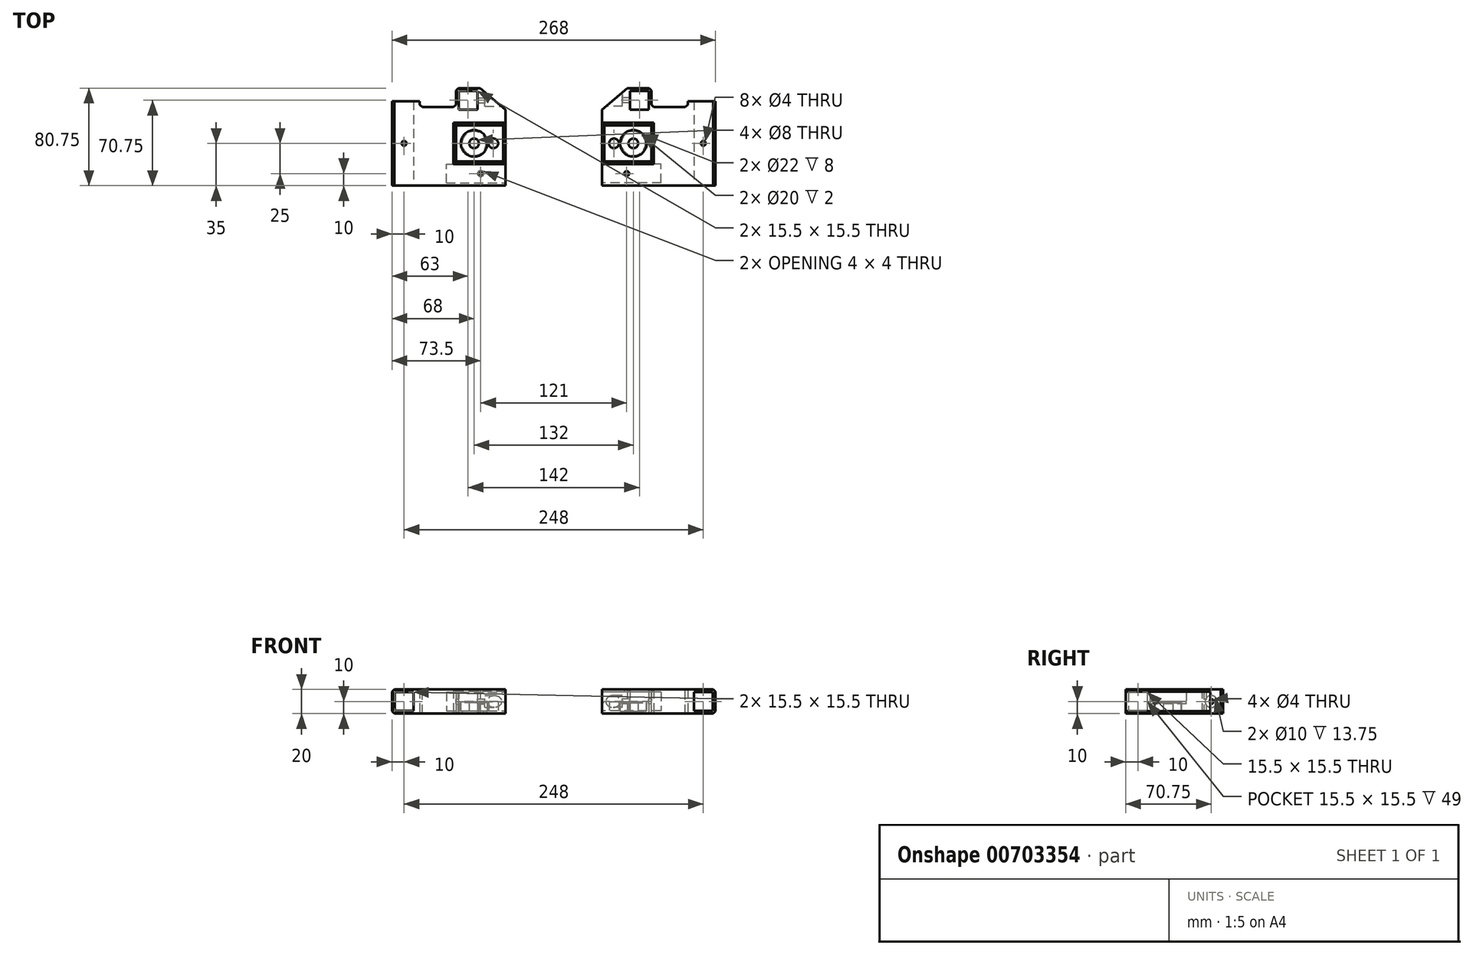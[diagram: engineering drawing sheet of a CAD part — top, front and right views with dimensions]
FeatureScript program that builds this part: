
annotation { "Feature Type Name" : "Feature", "Feature Type Description" : "" }
export const myFeature = defineFeature(function(context is Context, id is Id, definition is map)
    precondition{}
    {
        {
            var Q0;
            Q0=qCreatedBy(makeId("Top.planeOp"),FACE);
            var sketch = newSketch(context, id + "F0", { "sketchPlane" : qUnion([Q0])});
            skCircle(sketch, "E0", {"center": v(-50, 0) * mm, "radius": 4 * mm});
            skCircle(sketch, "E1", {"center": v(-66, 0) * mm, "radius": 4 * mm});
            skLineSegment(sketch, "E2.bottom", {"start": v(-81, 15) * mm, "end": v(-40, 15) * mm});
            skLineSegment(sketch, "E2.top", {"start": v(-81, -15) * mm, "end": v(-40, -15) * mm});
            skLineSegment(sketch, "E2.left", {"start": v(-81, 15) * mm, "end": v(-81, -15) * mm});
            skLineSegment(sketch, "E2.right", {"start": v(-40, 15) * mm, "end": v(-40, -15) * mm});
            skCircle(sketch, "E3", {"center": v(-66, 0) * mm, "radius": 11 * mm});
            skCircle(sketch, "E4", {"center": v(-66, 0) * mm, "radius": 10 * mm});
            skLineSegment(sketch, "E5", {"start": v(-81, 15) * mm, "end": v(-81, 35) * mm});
            skLineSegment(sketch, "E6", {"start": v(-81, -15) * mm, "end": v(-81, -35) * mm});
            skLineSegment(sketch, "E7", {"start": v(-81, -35) * mm, "end": v(-40, -35) * mm});
            skLineSegment(sketch, "E8", {"start": v(-40, -35) * mm, "end": v(-40, -15) * mm});
            skLineSegment(sketch, "E9.MirrorCS", {"start": v(-81, -35) * mm, "end": v(-40, -15) * mm, "construction": true});
            skCircle(sketch, "E10.MirrorC", {"center": v(-60.5, -25) * mm, "radius": 2 * mm});
            skLineSegment(sketch, "E11", {"start": v(-81, 35) * mm, "end": v(-134, 35) * mm});
            skLineSegment(sketch, "E12", {"start": v(-134, 35) * mm, "end": v(-134, -35) * mm});
            skLineSegment(sketch, "E13", {"start": v(-134, -35) * mm, "end": v(-81, -35) * mm});
            skLineSegment(sketch, "E14.bottom", {"start": v(-131.75, 7.75) * mm, "end": v(-116.25, 7.75) * mm});
            skLineSegment(sketch, "E14.top", {"start": v(-131.75, -7.75) * mm, "end": v(-116.25, -7.75) * mm});
            skLineSegment(sketch, "E14.left", {"start": v(-131.75, 7.75) * mm, "end": v(-131.75, -7.75) * mm});
            skLineSegment(sketch, "E14.right", {"start": v(-116.25, 7.75) * mm, "end": v(-116.25, -7.75) * mm});
            skPoint(sketch, "E14.middle", {"position": v(-124, 0) * mm});
            skCircle(sketch, "E15", {"center": v(-124, 0) * mm, "radius": 2 * mm});
            skLineSegment(sketch, "E16", {"start": v(-81, -15) * mm, "end": v(-40, -35) * mm, "construction": true});
            skLineSegment(sketch, "E17", {"start": v(-40, 15) * mm, "end": v(-40, 28) * mm});
            skLineSegment(sketch, "E18.top", {"start": v(-81, 45.75) * mm, "end": v(-61, 45.75) * mm});
            skLineSegment(sketch, "E18.left", {"start": v(-81, 35) * mm, "end": v(-81, 45.75) * mm});
            skLineSegment(sketch, "E18.right", {"start": v(-61, 28) * mm, "end": v(-61, 45.75) * mm});
            skLineSegment(sketch, "E19", {"start": v(-61, 28) * mm, "end": v(-40, 28) * mm});
            skLineSegment(sketch, "E20", {"start": v(-71, 45.75) * mm, "end": v(-71, 15) * mm, "construction": true});
            skLineSegment(sketch, "E21.bottom", {"start": v(-78.75, 43.5) * mm, "end": v(-63.25, 43.5) * mm});
            skLineSegment(sketch, "E21.top", {"start": v(-78.75, 28) * mm, "end": v(-63.25, 28) * mm});
            skLineSegment(sketch, "E21.left", {"start": v(-78.75, 43.5) * mm, "end": v(-78.75, 28) * mm});
            skLineSegment(sketch, "E21.right", {"start": v(-63.25, 43.5) * mm, "end": v(-63.25, 28) * mm});
            skPoint(sketch, "E21.middle", {"position": v(-71, 35.75) * mm});
            skLineSegment(sketch, "E22", {"start": v(-61, 45.75) * mm, "end": v(-40, 28) * mm});
            skLineSegment(sketch, "E23", {"start": v(-111, 35) * mm, "end": v(-111, 30) * mm});
            skLineSegment(sketch, "E24", {"start": v(-111, 30) * mm, "end": v(-81, 30) * mm});
            skSolve(sketch);
        }
        {
            var Q0;
            Q0=makeQuery(id+"F0.imprint","IMPRINT",FACE,{"disambiguationData":[TD([[makeQuery(id+"F0.imprint","IMPRINT",EDGE,{"derivedFrom":sQuery(id+"F0.wireOp",EDGE,"E0")}),-1.0]])]});
            extrude(context, id + "F1", {"entities" : qUnion([Q0]), "depth" : 10 * mm, "offsetDistance" : 25 * mm});
        }
        {
            var Q0;
            Q0=makeQuery(id+"F0.imprint","IMPRINT",FACE,{"disambiguationData":[TD([[makeQuery(id+"F0.imprint","IMPRINT",EDGE,{"derivedFrom":sQuery(id+"F0.wireOp",EDGE,"E2.bottom")}),1.0]])]});
            var Q1;
            Q1=makeQuery(id+"F0.imprint","IMPRINT",FACE,{"disambiguationData":[TD([[makeQuery(id+"F0.imprint","IMPRINT",EDGE,{"derivedFrom":sQuery(id+"F0.wireOp",EDGE,"E2.top")}),-1.0]])]});
            var Q2;
            Q2=makeQuery(id+"F0.imprint","IMPRINT",FACE,{"disambiguationData":[TD([[makeQuery(id+"F0.imprint","IMPRINT",EDGE,{"derivedFrom":sQuery(id+"F0.wireOp",EDGE,"E2.left")}),-1.0]])]});
            var Q3;
            Q3=makeQuery(id+"F0.imprint","IMPRINT",FACE,{"disambiguationData":[TD([[makeQuery(id+"F0.imprint","IMPRINT",EDGE,{"derivedFrom":sQuery(id+"F0.wireOp",EDGE,"E14.bottom")}),-1.0]])]});
            var Q4;
            {var subQ3=sQuery(id+"F0.wireOp",EDGE,"E18.bottom");Q4=makeQuery(id+"F0.imprint","IMPRINT",FACE,{"disambiguationData":[TD([[makeQuery(id+"F0.imprint","IMPRINT",EDGE,{"derivedFrom":subQ3}),1.0]])]});}
            var Q5;
            Q5=makeQuery(id+"F0.imprint","IMPRINT",FACE,{"disambiguationData":[TD([[makeQuery(id+"F0.imprint","IMPRINT",EDGE,{"derivedFrom":sQuery(id+"F0.wireOp",EDGE,"E18.right")}),-1.0]])]});
            extrude(context, id + "F2", {"entities" : qUnion([Q0, Q1, Q2, Q3, Q4, Q5]), "operationType" : NewBodyOperationType.ADD, "depth" : 20 * mm, "offsetDistance" : 25 * mm});
        }
        {
            var Q0;
            Q0=makeQuery(id+"F0.imprint","IMPRINT",FACE,{"disambiguationData":[TD([[makeQuery(id+"F0.imprint","IMPRINT",EDGE,{"derivedFrom":sQuery(id+"F0.wireOp",EDGE,"E3")}),1.0]])]});
            extrude(context, id + "F3", {"entities" : qUnion([Q0]), "operationType" : NewBodyOperationType.ADD, "depth" : 2 * mm, "offsetDistance" : 25 * mm});
        }
        {
            var Q0;
            Q0=makeQuery(id+"F1.opExtrude","SWEPT_FACE",FACE,{"disambiguationData":[OSD([sQuery(id+"F0.wireOp",EDGE,"E2.right"),sQuery(id+"F0.wireOp",EDGE,"lnFxAALh-jdBc-A6U8-vroT-Qa4E6eDd7EjD")])]});
            var sketch = newSketch(context, id + "F4", { "sketchPlane" : qUnion([Q0])});
            skPoint(sketch, "E25.MirrorP", {"position": v(-25, 10) * mm});
            skLineSegment(sketch, "E26.bottom", {"start": v(-32.75, 17.75) * mm, "end": v(-17.25, 17.75) * mm});
            skLineSegment(sketch, "E26.top", {"start": v(-32.75, 2.25) * mm, "end": v(-17.25, 2.25) * mm});
            skLineSegment(sketch, "E26.left", {"start": v(-32.75, 17.75) * mm, "end": v(-32.75, 2.25) * mm});
            skLineSegment(sketch, "E26.right", {"start": v(-17.25, 17.75) * mm, "end": v(-17.25, 2.25) * mm});
            skSolve(sketch);
        }
        {
            var Q0;
            Q0=makeQuery(id+"F4.imprint","IMPRINT",FACE,{"disambiguationData":[TD([[makeQuery(id+"F4.imprint","IMPRINT",EDGE,{"derivedFrom":sQuery(id+"F4.wireOp",EDGE,"jqq9uEYE-Uu8Z-dqdK-GRFn-HQd5PF9UBxML.bottom")}),-1.0]])]});
            var Q1;
            Q1=makeQuery(id+"F4.imprint","IMPRINT",FACE,{"disambiguationData":[TD([[makeQuery(id+"F4.imprint","IMPRINT",EDGE,{"derivedFrom":sQuery(id+"F4.wireOp",EDGE,"87533c7f-0075-4deb-97ef-fb3679262ebe1.MirrorCS")}),1.0]])]});
            var Q2;
            Q2=makeQuery(id+"F4.imprint","IMPRINT",FACE,{"disambiguationData":[TD([[makeQuery(id+"F4.imprint","IMPRINT",EDGE,{"derivedFrom":sQuery(id+"F4.wireOp",EDGE,"E26.bottom")}),-1.0]])]});
            extrude(context, id + "F5", {"entities" : qUnion([Q0, Q1, Q2]), "operationType" : NewBodyOperationType.REMOVE, "oppositeDirection" : true, "depth" : 49 * mm, "offsetDistance" : 25 * mm});
        }
        {
            var Q0;
            Q0=makeQuery(id+"F1.opExtrude","CAP_FACE",FACE,{"disambiguationData":[OSD([sQuery(id+"F0.wireOp",EDGE,"E0"),sQuery(id+"F0.wireOp",EDGE,"E2.top"),sQuery(id+"F0.wireOp",EDGE,"E2.left"),sQuery(id+"F0.wireOp",EDGE,"E2.right"),sQuery(id+"F0.wireOp",EDGE,"E3"),sQuery(id+"F0.wireOp",EDGE,"E5"),sQuery(id+"F0.wireOp",EDGE,"MvoQS5Ci-Blhk-AmRJ-KyyR-INJTXiuXo2vU"),sQuery(id+"F0.wireOp",EDGE,"lnFxAALh-jdBc-A6U8-vroT-Qa4E6eDd7EjD")])],"isStart":false});
            var sketch = newSketch(context, id + "F6", { "sketchPlane" : qUnion([Q0])});
            skCircle(sketch, "E27", {"center": v(-66, 0) * mm, "radius": 12.5 * mm});
            skSolve(sketch);
        }
        {
            var Q0;
            Q0=makeQuery(id+"F6.imprint","IMPRINT",FACE,{"disambiguationData":[TD([[makeQuery(id+"F6.imprint","IMPRINT",EDGE,{"derivedFrom":makeQuery(id+"F1.opExtrude","CAP_EDGE",EDGE,{"disambiguationData":[OSD([sQuery(id+"F0.wireOp",EDGE,"E3")])],"isStart":false})}),1.0]])]});
            extrude(context, id + "F7", {"entities" : qUnion([Q0]), "oppositeDirection" : true, "depth" : 8 * mm, "offsetDistance" : 25 * mm, "hasSecondDirection" : true, "secondDirectionOppositeDirection" : true, "secondDirectionDepth" : 1 * mm});
        }
        {
            var Q0;
            Q0=makeQuery(id+"F0.imprint","IMPRINT",FACE,{"disambiguationData":[TD([[makeQuery(id+"F0.imprint","IMPRINT",EDGE,{"derivedFrom":sQuery(id+"F0.wireOp",EDGE,"E1")}),1.0]])]});
            extrude(context, id + "F8", {"entities" : qUnion([Q0]), "operationType" : NewBodyOperationType.REMOVE, "depth" : 25 * mm, "offsetDistance" : 25 * mm});
        }
        {
            var Q0;
            Q0=makeQuery(id+"F2.opExtrude","SWEPT_FACE",FACE,{"disambiguationData":[OSD([sQuery(id+"F0.wireOp",EDGE,"E7"),sQuery(id+"F0.wireOp",EDGE,"E13")])]});
            var sketch = newSketch(context, id + "F9", { "sketchPlane" : qUnion([Q0])});
            skLineSegment(sketch, "E28.bottom", {"start": v(-116.25, 2.25) * mm, "end": v(-131.75, 2.25) * mm});
            skLineSegment(sketch, "E28.top", {"start": v(-116.25, 17.75) * mm, "end": v(-131.75, 17.75) * mm});
            skLineSegment(sketch, "E28.left", {"start": v(-116.25, 2.25) * mm, "end": v(-116.25, 17.75) * mm});
            skLineSegment(sketch, "E28.right", {"start": v(-131.75, 2.25) * mm, "end": v(-131.75, 17.75) * mm});
            skPoint(sketch, "E28.middle", {"position": v(-124, 10) * mm});
            skSolve(sketch);
        }
        {
            var Q0;
            Q0=makeQuery(id+"F9.imprint","IMPRINT",FACE,{"disambiguationData":[TD([[makeQuery(id+"F9.imprint","IMPRINT",EDGE,{"derivedFrom":sQuery(id+"F9.wireOp",EDGE,"E28.bottom")}),-1.0]])]});
            extrude(context, id + "F10", {"entities" : qUnion([Q0]), "operationType" : NewBodyOperationType.REMOVE, "endBound" : BoundingType.THROUGH_ALL, "oppositeDirection" : true, "depth" : 25 * mm, "offsetDistance" : 25 * mm});
        }
        {
            var Q0;
            Q0=makeQuery(id+"F2.opExtrude","CAP_EDGE",EDGE,{"disambiguationData":[OSD([sQuery(id+"F0.wireOp",EDGE,"E2.left")])],"isStart":false});
            var Q1;
            Q1=makeQuery(id+"F2.opExtrude","CAP_EDGE",EDGE,{"disambiguationData":[OSD([sQuery(id+"F0.wireOp",EDGE,"E2.bottom")])],"isStart":false});
            var Q2;
            Q2=makeQuery(id+"F2.opExtrude","CAP_EDGE",EDGE,{"disambiguationData":[OSD([sQuery(id+"F0.wireOp",EDGE,"E2.top")])],"isStart":false});
            var Q3;
            Q3=makeQuery(id+"F2.opExtrude","CAP_EDGE",EDGE,{"disambiguationData":[OSD([sQuery(id+"F0.wireOp",EDGE,"E12")])],"isStart":false});
            var Q4;
            Q4=makeQuery(id+"F2.opExtrude","CAP_EDGE",EDGE,{"disambiguationData":[OSD([sQuery(id+"F0.wireOp",EDGE,"E12")])],"isStart":true});
            var Q5;
            Q5=makeQuery(id+"F1.opExtrude","CAP_EDGE",EDGE,{"disambiguationData":[OSD([sQuery(id+"F0.wireOp",EDGE,"E2.right")])],"isStart":false});
            var Q6;
            Q6=makeQuery(id+"F2.opExtrude","SWEPT_EDGE",EDGE,{"disambiguationData":[OSD([sQuery(id+"F0.wireOp",EDGE,"E23"),sQuery(id+"F0.wireOp",EDGE,"E24")])]});
            var Q7;
            Q7=makeQuery(id+"F2.opExtrude","SWEPT_EDGE",EDGE,{"disambiguationData":[OSD([sQuery(id+"F0.wireOp",EDGE,"E5"),sQuery(id+"F0.wireOp",EDGE,"E24")])]});
            var Q8;
            Q8=makeQuery(id+"F2.opExtrude","SWEPT_EDGE",EDGE,{"disambiguationData":[OSD([sQuery(id+"F0.wireOp",EDGE,"E18.top"),sQuery(id+"F0.wireOp",EDGE,"E18.left")])]});
            chamfer(context, id + "F11", {"entities" : qUnion([Q0, Q1, Q2, Q3, Q4, Q5, Q6, Q7, Q8]), "width" : 2 * mm, "tangentPropagation" : true});
        }
        {
            var Q0;
            Q0=makeQuery(id+"F2.boolean.opBoolean","MERGE",FACE,{"derivedFrom":[makeQuery(id+"F1.opExtrude","SWEPT_FACE",FACE,{"disambiguationData":[OSD([sQuery(id+"F0.wireOp",EDGE,"E2.right")])]}),makeQuery(id+"F2.opExtrude","SWEPT_FACE",FACE,{"disambiguationData":[OSD([sQuery(id+"F0.wireOp",EDGE,"E8")])]}),makeQuery(id+"F2.opExtrude","SWEPT_FACE",FACE,{"disambiguationData":[OSD([sQuery(id+"F0.wireOp",EDGE,"E17")])]})]});
            var sketch = newSketch(context, id + "F12", { "sketchPlane" : qUnion([Q0])});
            skCircle(sketch, "E29", {"center": v(35.75, 10) * mm, "radius": 5 * mm});
            skCircle(sketch, "E30", {"center": v(35.75, 10) * mm, "radius": 2 * mm});
            skSolve(sketch);
        }
        {
            var Q0;
            Q0 = qSketchRegion(id + "F12", true);
            extrude(context, id + "F13", {"entities" : qUnion([Q0]), "operationType" : NewBodyOperationType.REMOVE, "oppositeDirection" : true, "depth" : 17 * mm, "offsetDistance" : 25 * mm});
        }
        {
            var Q0;
            Q0=makeQuery(id+"F12.imprint","IMPRINT",FACE,{"disambiguationData":[TD([[makeQuery(id+"F12.imprint","IMPRINT",EDGE,{"derivedFrom":sQuery(id+"F12.wireOp",EDGE,"E30")}),1.0]])]});
            extrude(context, id + "F14", {"entities" : qUnion([Q0]), "operationType" : NewBodyOperationType.REMOVE, "oppositeDirection" : true, "depth" : 41 * mm, "offsetDistance" : 25 * mm});
        }
        {
            var Q0;
            Q0=makeQuery(id+"F7.opExtrude","SWEPT_BODY",BODY,{"disambiguationData":[OSD([sQuery(id+"F0.wireOp",EDGE,"E3")])]});
            var Q1;
            Q1=makeQuery(id+"F1.opExtrude","SWEPT_BODY",BODY,{"disambiguationData":[OSD([sQuery(id+"F0.wireOp",EDGE,"E0"),sQuery(id+"F0.wireOp",EDGE,"E2.bottom"),sQuery(id+"F0.wireOp",EDGE,"E2.top"),sQuery(id+"F0.wireOp",EDGE,"E2.left"),sQuery(id+"F0.wireOp",EDGE,"E2.right"),sQuery(id+"F0.wireOp",EDGE,"E3")])]});
            var Q2;
            Q2=qCreatedBy(makeId("Right.planeOp"),FACE);
            mirror(context, id + "F15", {"entities" : qUnion([Q0, Q1]), "mirrorPlane" : qUnion([Q2])});
        }
    });
